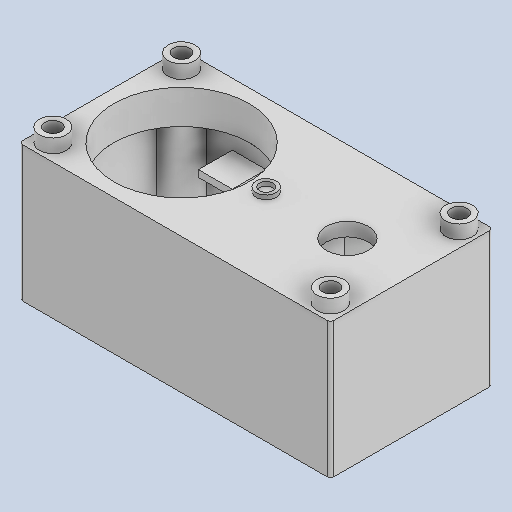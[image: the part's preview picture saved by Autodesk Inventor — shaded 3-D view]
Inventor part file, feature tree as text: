
AUTODESK INVENTOR PART (.ipt)
format: ipt  version: 2025.2 (Build 292293000, 293)  size: 165,888 bytes
history: native  units: mm
features: other x1, fillet x1
ambient origin geometry x8: Origin, YZ Plane, XZ Plane, XY Plane, X Axis, Y Axis, Z Axis, Center Point
bodies: Body1 (feature_tree)
feature tree (2):
  other  "Bryła1"
  fillet  "Fillet1"  [1 undecoded]
note: 1 required parameter value undecoded (feature->parameter linkage not recoverable at this tier; creation-order binding heuristic only, values carry confidence <= 0.55)
